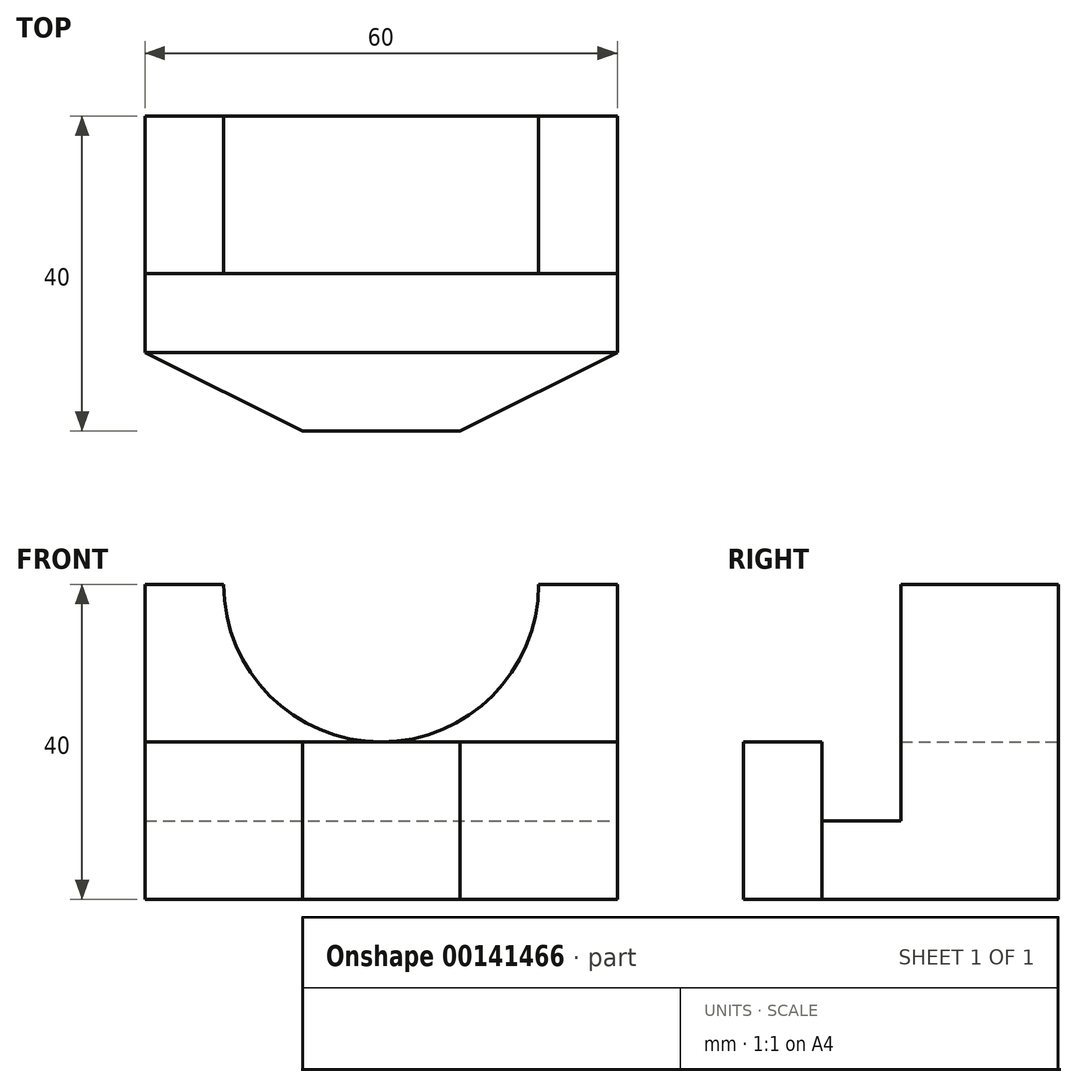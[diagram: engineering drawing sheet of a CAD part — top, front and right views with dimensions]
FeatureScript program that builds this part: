
annotation { "Feature Type Name" : "Feature", "Feature Type Description" : "" }
export const myFeature = defineFeature(function(context is Context, id is Id, definition is map)
    precondition{}
    {
        {
            var Q0;
            Q0=qCreatedBy(makeId("Front.planeOp"),FACE);
            var sketch = newSketch(context, id + "F0", { "sketchPlane" : qUnion([Q0])});
            skLineSegment(sketch, "E0", {"start": v(0, 0) * mm, "end": v(60, 0) * mm});
            skLineSegment(sketch, "E1", {"start": v(60, 0) * mm, "end": v(60, 40) * mm});
            skLineSegment(sketch, "E2", {"start": v(60, 40) * mm, "end": v(50, 40) * mm});
            skLineSegment(sketch, "E3", {"start": v(0, 0) * mm, "end": v(0, 40) * mm});
            skLineSegment(sketch, "E4", {"start": v(0, 40) * mm, "end": v(10, 40) * mm});
            skLineSegment(sketch, "E5", {"start": v(0, 20) * mm, "end": v(60, 20) * mm});
            skArc(sketch, "E6", {"start": v(10, 40) * mm, "mid": v(30, 20) * mm, "end": v(50, 40) * mm});
            skPoint(sketch, "E6.centerSnap0", {"position": v(30, 20) * mm});
            skLineSegment(sketch, "E7", {"start": v(10, 40) * mm, "end": v(50, 40) * mm, "construction": true});
            skLineSegment(sketch, "E8", {"start": v(30, 40) * mm, "end": v(30, 20) * mm, "construction": true});
            skSolve(sketch);
        }
        {
            var Q0;
            Q0 = qSketchRegion(id + "F0", true);
            extrude(context, id + "F1", {"entities" : qUnion([Q0]), "depth" : 40 * mm});
        }
        {
            var Q0;
            Q0=makeQuery(id+"F1.opExtrude","SWEPT_FACE",FACE,{"disambiguationData":[OSD([sQuery(id+"F0.wireOp",EDGE,"E1")])]});
            var sketch = newSketch(context, id + "F2", { "sketchPlane" : qUnion([Q0])});
            skLineSegment(sketch, "E9", {"start": v(-40, 40) * mm, "end": v(-20, 40) * mm});
            skLineSegment(sketch, "E10", {"start": v(-20, 40) * mm, "end": v(-20, 10) * mm});
            skLineSegment(sketch, "E11", {"start": v(-20, 10) * mm, "end": v(-30, 10) * mm});
            skLineSegment(sketch, "E12", {"start": v(-30, 10) * mm, "end": v(-30, 20) * mm});
            skLineSegment(sketch, "E13", {"start": v(-30, 20) * mm, "end": v(-40, 20) * mm});
            skLineSegment(sketch, "E14", {"start": v(-40, 20) * mm, "end": v(-40, 40) * mm});
            skSolve(sketch);
        }
        {
            var Q0;
            Q0=makeQuery(id+"F2.imprint","IMPRINT",FACE,{"disambiguationData":[TD([[makeQuery(id+"F2.imprint","IMPRINT",EDGE,{"derivedFrom":sQuery(id+"F2.wireOp",EDGE,"E9")}),-1.0]])]});
            extrude(context, id + "F3", {"entities" : qUnion([Q0]), "operationType" : NewBodyOperationType.REMOVE, "oppositeDirection" : true, "depth" : 60 * mm});
        }
        {
            var Q0;
            Q0=makeQuery(id+"F3.boolean.opBoolean","COPY",FACE,{"derivedFrom":makeQuery(id+"F3.opExtrude","SWEPT_FACE",FACE,{"disambiguationData":[OSD([sQuery(id+"F2.wireOp",EDGE,"E13")])]})});
            var sketch = newSketch(context, id + "F4", { "sketchPlane" : qUnion([Q0])});
            skLineSegment(sketch, "E15", {"start": v(0, -30) * mm, "end": v(20, -30) * mm});
            skLineSegment(sketch, "E16", {"start": v(20, -30) * mm, "end": v(20, -40) * mm});
            skLineSegment(sketch, "E17", {"start": v(60, -30) * mm, "end": v(40, -30) * mm});
            skLineSegment(sketch, "E18", {"start": v(40, -30) * mm, "end": v(40, -40) * mm});
            skLineSegment(sketch, "E19", {"start": v(0, -30) * mm, "end": v(20, -40) * mm});
            skLineSegment(sketch, "E20", {"start": v(40, -40) * mm, "end": v(60, -30) * mm});
            skSolve(sketch);
        }
        {
            var Q0;
            {var subQ0=sQuery(id+"F4.wireOp",EDGE,"E19");Q0=makeQuery(id+"F4.imprint","IMPRINT",FACE,{"disambiguationData":[TD([[makeQuery(id+"F4.imprint","IMPRINT",EDGE,{"derivedFrom":subQ0}),-1.0]])]});}
            var Q1;
            {var subQ0=sQuery(id+"F4.wireOp",EDGE,"E20");Q1=makeQuery(id+"F4.imprint","IMPRINT",FACE,{"disambiguationData":[TD([[makeQuery(id+"F4.imprint","IMPRINT",EDGE,{"derivedFrom":subQ0}),-1.0]])]});}
            extrude(context, id + "F5", {"entities" : qUnion([Q0, Q1]), "operationType" : NewBodyOperationType.REMOVE, "oppositeDirection" : true, "depth" : 25 * mm});
        }
    });
